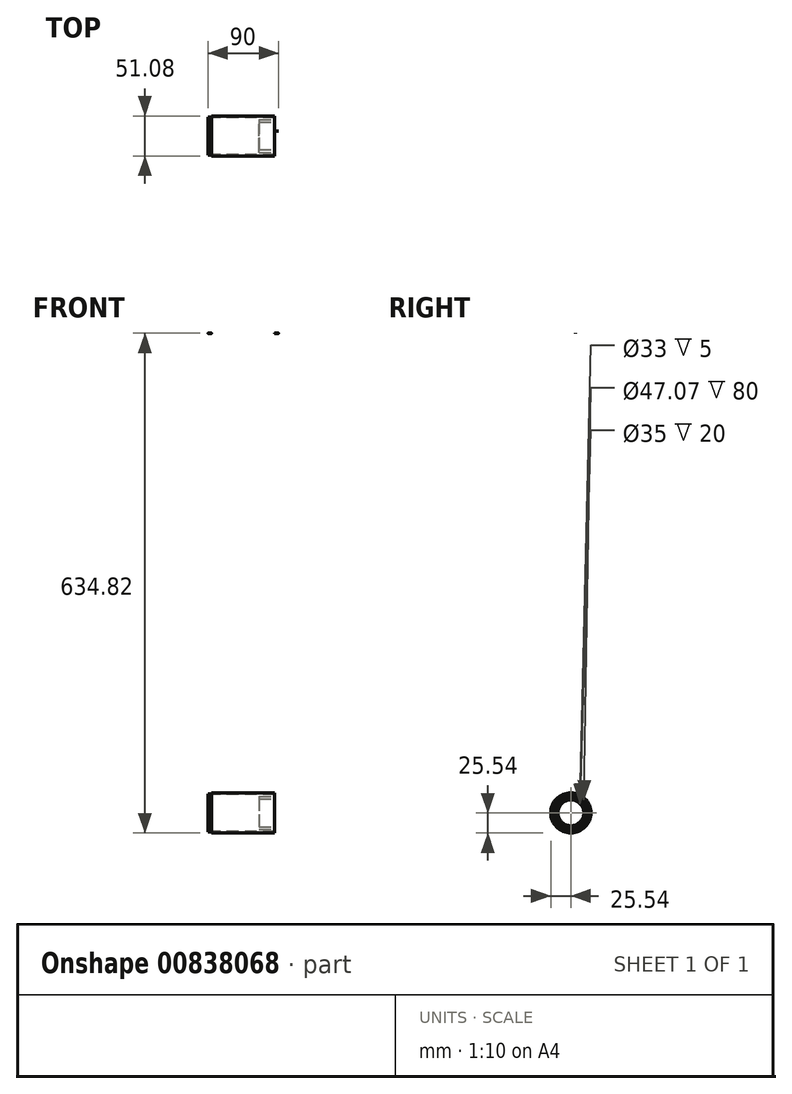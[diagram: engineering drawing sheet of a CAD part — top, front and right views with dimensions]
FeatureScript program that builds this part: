
annotation { "Feature Type Name" : "Feature", "Feature Type Description" : "" }
export const myFeature = defineFeature(function(context is Context, id is Id, definition is map)
    precondition{}
    {
        {
            var Q0;
            Q0=qCreatedBy(makeId("Right.planeOp"),FACE);
            var sketch = newSketch(context, id + "F0", { "sketchPlane" : qUnion([Q0])});
            skCircle(sketch, "E0", {"center": v(0, 0) * mm, "radius": 25.54 * mm});
            skCircle(sketch, "E1", {"center": v(0, 0) * mm, "radius": 23.54 * mm});
            skSolve(sketch);
        }
        {
            var Q0;
            Q0 = qSketchRegion(id + "F0", true);
            extrude(context, id + "F1", {"entities" : qUnion([Q0]), "depth" : 80 * mm, "offsetDistance" : 25 * mm});
        }
        {
            var Q0;
            Q0=makeQuery(id+"F1.opExtrude","CAP_FACE",FACE,{"disambiguationData":[OSD([sQuery(id+"F0.wireOp",EDGE,"E0"),sQuery(id+"F0.wireOp",EDGE,"E1")])],"isStart":true});
            var sketch = newSketch(context, id + "F2", { "sketchPlane" : qUnion([Q0])});
            skCircle(sketch, "E2", {"center": v(0, 0) * mm, "radius": 24 * mm});
            skLineSegment(sketch, "E3", {"start": v(0, 25.54) * mm, "end": v(0, 609.1) * mm, "construction": true});
            skArc(sketch, "E4", {"start": v(6, 609.28) * mm, "mid": v(-0.09, 615.1) * mm, "end": v(-6, 609.1) * mm});
            skArc(sketch, "E5", {"start": v(3, 609.1) * mm, "mid": v(0, 612.1) * mm, "end": v(-3, 609.1) * mm});
            skLineSegment(sketch, "E6", {"start": v(-6, 609.28) * mm, "end": v(-6, 609.1) * mm});
            skLineSegment(sketch, "E7", {"start": v(6, 609.28) * mm, "end": v(23.73, 9.43) * mm});
            skLineSegment(sketch, "E8", {"start": v(-1.33, 603.1) * mm, "end": v(-2.15, 603.1) * mm});
            skLineSegment(sketch, "E9", {"start": v(-3, 609.1) * mm, "end": v(-6, 609.1) * mm});
            skLineSegment(sketch, "E10.trimOffspring", {"start": v(-6.32, 598.25) * mm, "end": v(-23.73, 9.43) * mm});
            skArc(sketch, "E11", {"start": v(2.47, 606.2) * mm, "mid": v(2.89, 607.62) * mm, "end": v(3, 609.1) * mm});
            skPoint(sketch, "E12.visualSharp", {"position": v(-6.18, 603.1) * mm});
            skArc(sketch, "E12.filletArc", {"start": v(-1.33, 603.1) * mm, "mid": v(-4.8, 601.69) * mm, "end": v(-6.32, 598.25) * mm});
            skPoint(sketch, "E13.visualSharp", {"position": v(0, 603.1) * mm});
            skArc(sketch, "E13.filletArc", {"start": v(-2.15, 603.1) * mm, "mid": v(0.63, 603.95) * mm, "end": v(2.47, 606.2) * mm});
            skSolve(sketch);
        }
        {
            var Q0;
            Q0 = qSketchRegion(id + "F2", true);
            extrude(context, id + "F3", {"entities" : qUnion([Q0]), "depth" : 5 * mm, "offsetDistance" : 25 * mm});
        }
        {
            var Q0;
            Q0=makeQuery(id+"F3.opExtrude","CAP_FACE",FACE,{"disambiguationData":[OSD([sQuery(id+"F2.wireOp",EDGE,"E2"),sQuery(id+"F2.wireOp",EDGE,"E4"),sQuery(id+"F2.wireOp",EDGE,"E5"),sQuery(id+"F2.wireOp",EDGE,"E6"),sQuery(id+"F2.wireOp",EDGE,"E7"),sQuery(id+"F2.wireOp",EDGE,"E8"),sQuery(id+"F2.wireOp",EDGE,"E9"),sQuery(id+"F2.wireOp",EDGE,"E10.trimOffspring"),sQuery(id+"F2.wireOp",EDGE,"E11"),sQuery(id+"F2.wireOp",EDGE,"E12.filletArc"),sQuery(id+"F2.wireOp",EDGE,"E13.filletArc")])],"isStart":true});
            cPlane(context, id + "F4", {"entities" : qUnion([Q0]), "cplaneType" : CPlaneType.OFFSET, "offset" : 40 * mm, "width" : 150 * mm, "height" : 150 * mm});
        }
        {
            var Q0;
            Q0=makeQuery(id+"F3.opExtrude","SWEPT_BODY",BODY,{"disambiguationData":[OSD([sQuery(id+"F2.wireOp",EDGE,"E2"),sQuery(id+"F2.wireOp",EDGE,"E4"),sQuery(id+"F2.wireOp",EDGE,"E5"),sQuery(id+"F2.wireOp",EDGE,"E6"),sQuery(id+"F2.wireOp",EDGE,"E7"),sQuery(id+"F2.wireOp",EDGE,"E8"),sQuery(id+"F2.wireOp",EDGE,"E9"),sQuery(id+"F2.wireOp",EDGE,"E10.trimOffspring"),sQuery(id+"F2.wireOp",EDGE,"E11"),sQuery(id+"F2.wireOp",EDGE,"E12.filletArc"),sQuery(id+"F2.wireOp",EDGE,"E13.filletArc")])]});
            var Q1;
            Q1=qCreatedBy(id+"F4.planeOp",FACE);
            mirror(context, id + "F5", {"entities" : qUnion([Q0]), "mirrorPlane" : qUnion([Q1])});
        }
        {
            var Q0;
            Q0=makeQuery(id+"F5.opPattern","COPY",FACE,{"derivedFrom":makeQuery(id+"F3.opExtrude","CAP_FACE",FACE,{"disambiguationData":[OSD([sQuery(id+"F2.wireOp",EDGE,"E2"),sQuery(id+"F2.wireOp",EDGE,"E4"),sQuery(id+"F2.wireOp",EDGE,"E5"),sQuery(id+"F2.wireOp",EDGE,"E6"),sQuery(id+"F2.wireOp",EDGE,"E7"),sQuery(id+"F2.wireOp",EDGE,"E8"),sQuery(id+"F2.wireOp",EDGE,"E9"),sQuery(id+"F2.wireOp",EDGE,"E10.trimOffspring"),sQuery(id+"F2.wireOp",EDGE,"E11"),sQuery(id+"F2.wireOp",EDGE,"E12.filletArc"),sQuery(id+"F2.wireOp",EDGE,"E13.filletArc")])],"isStart":true}),"instanceName":"1"});
            var sketch = newSketch(context, id + "F6", { "sketchPlane" : qUnion([Q0])});
            skCircle(sketch, "E14", {"center": v(0, 0) * mm, "radius": 20.75 * mm});
            skCircle(sketch, "E15", {"center": v(0, 0) * mm, "radius": 17.5 * mm});
            skSolve(sketch);
        }
        {
            var Q0;
            Q0 = qSketchRegion(id + "F6", true);
            extrude(context, id + "F7", {"entities" : qUnion([Q0]), "operationType" : NewBodyOperationType.ADD, "depth" : 20 * mm, "offsetDistance" : 25 * mm});
        }
        {
            var Q0;
            Q0=makeQuery(id+"F3.opExtrude","CAP_FACE",FACE,{"disambiguationData":[OSD([sQuery(id+"F2.wireOp",EDGE,"E2"),sQuery(id+"F2.wireOp",EDGE,"E4"),sQuery(id+"F2.wireOp",EDGE,"E5"),sQuery(id+"F2.wireOp",EDGE,"E6"),sQuery(id+"F2.wireOp",EDGE,"E7"),sQuery(id+"F2.wireOp",EDGE,"E8"),sQuery(id+"F2.wireOp",EDGE,"E9"),sQuery(id+"F2.wireOp",EDGE,"E10.trimOffspring"),sQuery(id+"F2.wireOp",EDGE,"E11"),sQuery(id+"F2.wireOp",EDGE,"E12.filletArc"),sQuery(id+"F2.wireOp",EDGE,"E13.filletArc")])],"isStart":false});
            var sketch = newSketch(context, id + "F8", { "sketchPlane" : qUnion([Q0])});
            skLineSegment(sketch, "E16", {"start": v(-12.52, 25.54) * mm, "end": v(12.52, 25.54) * mm});
            skLineSegment(sketch, "E17", {"start": v(15.47, 29.05) * mm, "end": v(10.9, 55.05) * mm});
            skLineSegment(sketch, "E18", {"start": v(1.48, 94.33) * mm, "end": v(-1.48, 94.33) * mm});
            skLineSegment(sketch, "E19", {"start": v(-4.44, 91.85) * mm, "end": v(-9.14, 65.05) * mm});
            skLineSegment(sketch, "E20", {"start": v(-6.19, 61.54) * mm, "end": v(6.19, 61.54) * mm});
            skLineSegment(sketch, "E21", {"start": v(-7.95, 57.54) * mm, "end": v(7.95, 57.54) * mm});
            skLineSegment(sketch, "E22.trimOffspring", {"start": v(-10.9, 55.05) * mm, "end": v(-15.47, 29.05) * mm});
            skLineSegment(sketch, "E23.trimOffspring", {"start": v(9.14, 65.05) * mm, "end": v(4.44, 91.85) * mm});
            skPoint(sketch, "E24.visualSharp", {"position": v(4, 94.33) * mm});
            skArc(sketch, "E24.filletArc", {"start": v(4.44, 91.85) * mm, "mid": v(3.41, 93.63) * mm, "end": v(1.48, 94.33) * mm});
            skPoint(sketch, "E25.visualSharp", {"position": v(-4, 94.33) * mm});
            skArc(sketch, "E25.filletArc", {"start": v(-1.48, 94.33) * mm, "mid": v(-3.41, 93.63) * mm, "end": v(-4.44, 91.85) * mm});
            skPoint(sketch, "E26.visualSharp", {"position": v(9.76, 61.54) * mm});
            skArc(sketch, "E26.filletArc", {"start": v(6.19, 61.54) * mm, "mid": v(8.49, 62.6) * mm, "end": v(9.14, 65.05) * mm});
            skPoint(sketch, "E27.visualSharp", {"position": v(-9.76, 61.54) * mm});
            skArc(sketch, "E27.filletArc", {"start": v(-9.14, 65.05) * mm, "mid": v(-8.49, 62.6) * mm, "end": v(-6.19, 61.54) * mm});
            skPoint(sketch, "E28.visualSharp", {"position": v(-10.47, 57.54) * mm});
            skArc(sketch, "E28.filletArc", {"start": v(-7.95, 57.54) * mm, "mid": v(-9.88, 56.83) * mm, "end": v(-10.9, 55.05) * mm});
            skPoint(sketch, "E29.visualSharp", {"position": v(10.47, 57.54) * mm});
            skArc(sketch, "E29.filletArc", {"start": v(10.9, 55.05) * mm, "mid": v(9.88, 56.83) * mm, "end": v(7.95, 57.54) * mm});
            skPoint(sketch, "E30.visualSharp", {"position": v(16.09, 25.54) * mm});
            skArc(sketch, "E30.filletArc", {"start": v(12.52, 25.54) * mm, "mid": v(14.81, 26.6) * mm, "end": v(15.47, 29.05) * mm});
            skPoint(sketch, "E31.visualSharp", {"position": v(-16.09, 25.54) * mm});
            skArc(sketch, "E31.filletArc", {"start": v(-15.47, 29.05) * mm, "mid": v(-14.81, 26.6) * mm, "end": v(-12.52, 25.54) * mm});
            skSolve(sketch);
        }
        {
            var Q0;
            Q0 = qSketchRegion(id + "F8", true);
            extrude(context, id + "F9", {"entities" : qUnion([Q0]), "operationType" : NewBodyOperationType.REMOVE, "endBound" : BoundingType.THROUGH_ALL, "oppositeDirection" : true, "depth" : 25 * mm, "offsetDistance" : 25 * mm});
        }
        {
            var Q0;
            Q0=makeQuery(id+"F5.opPattern","COPY",FACE,{"derivedFrom":makeQuery(id+"F3.opExtrude","CAP_FACE",FACE,{"disambiguationData":[OSD([sQuery(id+"F2.wireOp",EDGE,"E2"),sQuery(id+"F2.wireOp",EDGE,"E4"),sQuery(id+"F2.wireOp",EDGE,"E5"),sQuery(id+"F2.wireOp",EDGE,"E6"),sQuery(id+"F2.wireOp",EDGE,"E7"),sQuery(id+"F2.wireOp",EDGE,"E8"),sQuery(id+"F2.wireOp",EDGE,"E9"),sQuery(id+"F2.wireOp",EDGE,"E10.trimOffspring"),sQuery(id+"F2.wireOp",EDGE,"E11"),sQuery(id+"F2.wireOp",EDGE,"E12.filletArc"),sQuery(id+"F2.wireOp",EDGE,"E13.filletArc")])],"isStart":false}),"instanceName":"1"});
            var sketch = newSketch(context, id + "F10", { "sketchPlane" : qUnion([Q0])});
            skCircle(sketch, "E32", {"center": v(0, 0) * mm, "radius": 16.5 * mm});
            skSolve(sketch);
        }
        {
            var Q0;
            Q0 = qSketchRegion(id + "F10", true);
            extrude(context, id + "F11", {"entities" : qUnion([Q0]), "operationType" : NewBodyOperationType.REMOVE, "endBound" : BoundingType.THROUGH_ALL, "oppositeDirection" : true, "depth" : 25 * mm, "offsetDistance" : 25 * mm});
        }
    });
